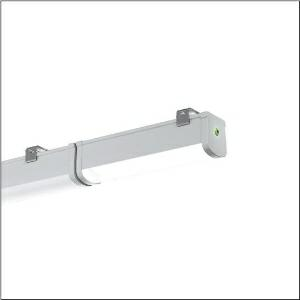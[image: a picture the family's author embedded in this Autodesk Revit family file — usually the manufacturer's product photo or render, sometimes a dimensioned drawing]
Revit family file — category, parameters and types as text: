
# Revit family: monsun_r__31_58fa207a403b3g_c1e4
name_source: partatom
category: Lighting Fixtures
units: mm (PartAtom-declared; Revit-internal decimal feet)

## family parameters
Cut with Voids When Loaded = No
Host = Face
Light Source = No
Part Type = Normal
Room Calculation Point = No
Round Connector Dimension = Use Diameter
Shared = No

## types (1)
- --- (1 x LED, 450 lm, 5 W, 4000K)
    Apparent Load = 5 VA
    CIE Flux Codes = 42 72 91 92 100
    Color Rendering = 80
    Color Temperature = 4000K
    Default Elevation = 1800 mm
    Description = Monsun® 31, emergency light element, primary optical cover: diffuser, of PC, frosted, light emission: direct distribution, primary light characteristic: symmetric, installation type: surface-mounted, EM-KIT 3h,LED, rated luminous flux: 450lm, luminous efficacy: 100lm/W, light colour: 840, colour temperature: 4000K, control gear: ON/OFF, emergency light function, with socket/plug, mains connection: 220..240V, AC, 50..60Hz, rated input power: 5W, housing, luminaire housing, of PC, light grey (RAL 7035), length: 297mm, width: 68mm, height: 76mm, protection rating (complete): IP65, insulation class (complete): insulation class II (safety insulation), certification: CE, protection symbol: D, impact resistance: IK08, permissible operating ambient temperature: 0..+40°C, standard: EN 60598-2-22, corresponds to IFS (International Featured Standards) requirements for safety and quality in the food industry, packaging unit: 1 piece
    Height = 77 mm
    Lamp = 1 x LED
    Lamp Light Flux = 450 lm
    Lamp Power = 5 W
    Lamp count = 1
    Length = 294 mm
    Luminous efficacy = 90 lm/W
    Manufacturer = Siteco
    ModVariant = No
    Model = 58FA207A403B3G
    Mounting Place = Ceiling
    Mounting Type = Surface mounted
    Number of Poles = 1
    OnlyDefault = Yes
    Power Factor = 1
    Product Name = Monsun® 31
    Product group = emergency light element
    ProductGroupID = 309
    Protection Class = Protection class II
    Protection Degree = IP 65
    RLX_Detail_Level = 1
    RLX_Emergency_Light_Flux = 0 lm
    RLX_Emergency_Type = 0
    RLX_Emergency_Type_DB = No
    RlxData = <blob elided: 31141 chars, md5=f64089f9>
    Socket = socket
    Standby Power = 0 W
    System Light Flux = 450 lm
    System Power = 5 W
    Type Comments = : 3 h
    Type Image = l_1006658.jpg
    URL = http://relux.com
    VarID = @adj_218807
    Voltage = 0 V
    Weight = 0.00 kg
    Width = 69 mm

## geometry (parser evidence)
native form markers: Blend x4, Sweep x12
no freeform markers — native parametric forms only
